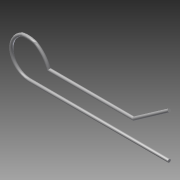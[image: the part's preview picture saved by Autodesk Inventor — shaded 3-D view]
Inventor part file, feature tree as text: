
AUTODESK INVENTOR PART (.ipt)
format: ipt  version: 2013 (Build 170138000, 138)  size: 104,448 bytes
history: native  units: in
note: dims shown in document units (in); Inventor stores cm internally (conversion verified against a paired STEP export)
features: sketch x2, sweep x1
ambient origin geometry x8: Origin, YZ Plane, XZ Plane, XY Plane, X Axis, Y Axis, Z Axis, Center Point
bodies: Solid1 (feature_tree)
feature tree (3):
  sweep  "Sweep1"
  sketch  "Sketch1"  dims[d0=0.6in d2=0.45in]
  sketch  "Sketch2"  dims[d3=0.2405in d4=0.0025in d5=0.0in]
